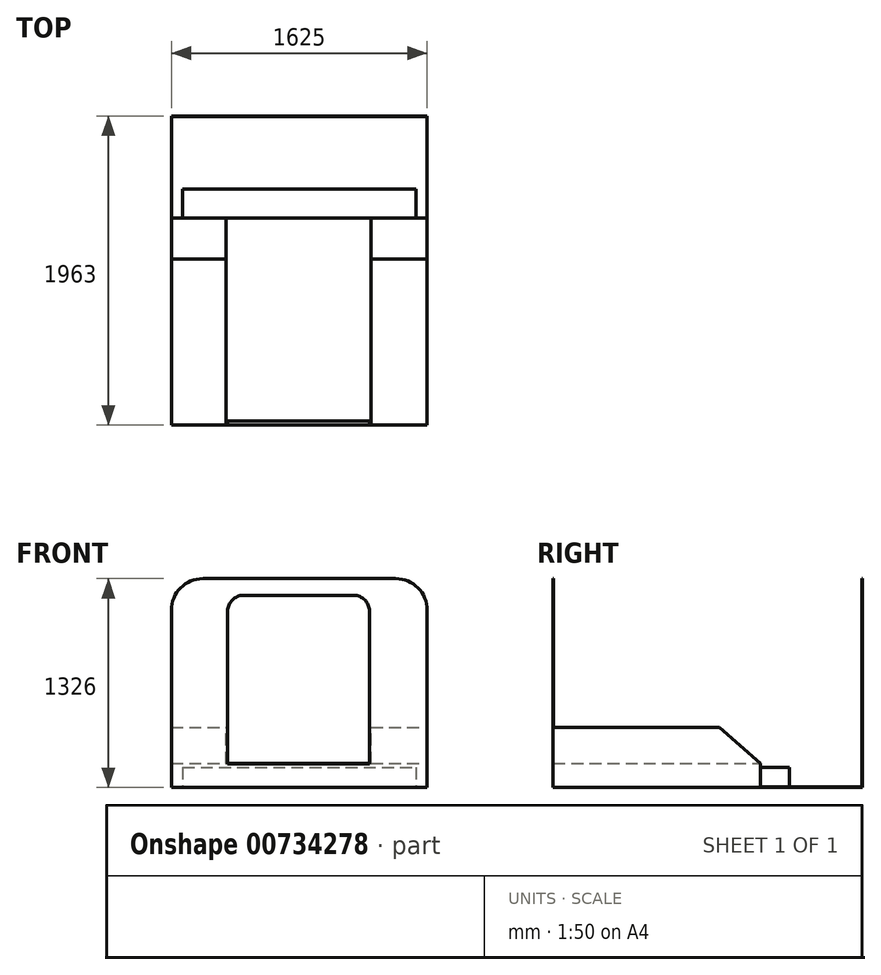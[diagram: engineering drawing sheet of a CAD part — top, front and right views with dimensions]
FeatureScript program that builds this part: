
annotation { "Feature Type Name" : "Feature", "Feature Type Description" : "" }
export const myFeature = defineFeature(function(context is Context, id is Id, definition is map)
    precondition{}
    {
        {
            var Q0;
            Q0=qCreatedBy(makeId("Top.planeOp"),FACE);
            var sketch = newSketch(context, id + "F0", { "sketchPlane" : qUnion([Q0])});
            skLineSegment(sketch, "E0.bottom", {"start": v(0, 0) * mm, "end": v(1625, 0) * mm});
            skLineSegment(sketch, "E0.top", {"start": v(0, 1960) * mm, "end": v(1625, 1960) * mm});
            skLineSegment(sketch, "E0.left", {"start": v(0, 0) * mm, "end": v(0, 1960) * mm});
            skLineSegment(sketch, "E0.right", {"start": v(1625, 0) * mm, "end": v(1625, 1960) * mm});
            skSolve(sketch);
        }
        {
            var Q0;
            Q0 = qSketchRegion(id + "F0", true);
            extrude(context, id + "F1", {"entities" : qUnion([Q0]), "depth" : 380 * mm, "offsetDistance" : 25 * mm});
        }
        {
            var Q0;
            Q0=makeQuery(id+"F1.opExtrude","CAP_FACE",FACE,{"disambiguationData":[OSD([sQuery(id+"F0.wireOp",EDGE,"E0.bottom"),sQuery(id+"F0.wireOp",EDGE,"E0.top"),sQuery(id+"F0.wireOp",EDGE,"E0.left"),sQuery(id+"F0.wireOp",EDGE,"E0.right")])],"isStart":false});
            var sketch = newSketch(context, id + "F2", { "sketchPlane" : qUnion([Q0])});
            skLineSegment(sketch, "E1.bottom", {"start": v(348, 0) * mm, "end": v(1268, 0) * mm});
            skLineSegment(sketch, "E1.top", {"start": v(348, 1960) * mm, "end": v(1268, 1960) * mm});
            skLineSegment(sketch, "E1.left", {"start": v(348, 0) * mm, "end": v(348, 1960) * mm});
            skLineSegment(sketch, "E1.right", {"start": v(1268, 0) * mm, "end": v(1268, 1960) * mm});
            skSolve(sketch);
        }
        {
            var Q0;
            Q0 = qSketchRegion(id + "F2", true);
            extrude(context, id + "F3", {"entities" : qUnion([Q0]), "operationType" : NewBodyOperationType.REMOVE, "oppositeDirection" : true, "depth" : 228 * mm, "offsetDistance" : 25 * mm});
        }
        {
            var Q0;
            {var subQ0=sQuery(id+"F0.wireOp",EDGE,"E0.bottom");var subQ1=sQuery(id+"F0.wireOp",EDGE,"E0.top");var subQ2=sQuery(id+"F0.wireOp",EDGE,"E0.left");Q0=makeQuery(id+"F3.boolean.opBoolean","SPLIT",FACE,{"disambiguationData":[TD([makeQuery(id+"F1.opExtrude","SWEPT_FACE",FACE,{"disambiguationData":[OSD([subQ2])]})])],"derivedFrom":makeQuery(id+"F1.opExtrude","CAP_FACE",FACE,{"disambiguationData":[OSD([subQ0,subQ1,subQ2,sQuery(id+"F0.wireOp",EDGE,"E0.right")])],"isStart":false})});}
            var sketch = newSketch(context, id + "F4", { "sketchPlane" : qUnion([Q0])});
            skLineSegment(sketch, "E2.bottom", {"start": v(0, 1960) * mm, "end": v(1625, 1960) * mm});
            skLineSegment(sketch, "E2.top", {"start": v(0, 1315) * mm, "end": v(1625, 1315) * mm});
            skLineSegment(sketch, "E2.left", {"start": v(0, 1960) * mm, "end": v(0, 1315) * mm});
            skLineSegment(sketch, "E2.right", {"start": v(1625, 1960) * mm, "end": v(1625, 1315) * mm});
            skSolve(sketch);
        }
        {
            var Q0;
            Q0 = qSketchRegion(id + "F4", true);
            extrude(context, id + "F5", {"entities" : qUnion([Q0]), "operationType" : NewBodyOperationType.REMOVE, "oppositeDirection" : true, "depth" : 378 * mm, "offsetDistance" : 25 * mm});
        }
        {
            var Q0;
            Q0=makeQuery(id+"F5.boolean.opBoolean","COPY",FACE,{"derivedFrom":makeQuery(id+"F5.opExtrude","CAP_FACE",FACE,{"disambiguationData":[OSD([sQuery(id+"F4.wireOp",EDGE,"E2.bottom"),sQuery(id+"F4.wireOp",EDGE,"E2.top"),sQuery(id+"F4.wireOp",EDGE,"E2.left"),sQuery(id+"F4.wireOp",EDGE,"E2.right")])],"isStart":false})});
            var sketch = newSketch(context, id + "F6", { "sketchPlane" : qUnion([Q0])});
            skLineSegment(sketch, "E3.bottom", {"start": v(72.5, 1315) * mm, "end": v(1552.5, 1315) * mm});
            skLineSegment(sketch, "E3.top", {"start": v(72.5, 1500) * mm, "end": v(1552.5, 1500) * mm});
            skLineSegment(sketch, "E3.left", {"start": v(72.5, 1315) * mm, "end": v(72.5, 1500) * mm});
            skLineSegment(sketch, "E3.right", {"start": v(1552.5, 1315) * mm, "end": v(1552.5, 1500) * mm});
            skSolve(sketch);
        }
        {
            var Q0;
            Q0 = qSketchRegion(id + "F6", true);
            extrude(context, id + "F7", {"entities" : qUnion([Q0]), "operationType" : NewBodyOperationType.ADD, "depth" : 125 * mm, "offsetDistance" : 25 * mm});
        }
        {
            var Q0;
            Q0=makeQuery(id+"F1.opExtrude","SWEPT_FACE",FACE,{"disambiguationData":[OSD([sQuery(id+"F0.wireOp",EDGE,"E0.top")])]});
            var sketch = newSketch(context, id + "F8", { "sketchPlane" : qUnion([Q0])});
            skLineSegment(sketch, "E4.bottom", {"start": v(-1625, 0) * mm, "end": v(0, 0) * mm});
            skLineSegment(sketch, "E4.top", {"start": v(-1425, 1326) * mm, "end": v(-200, 1326) * mm});
            skLineSegment(sketch, "E4.left", {"start": v(-1625, 0) * mm, "end": v(-1625, 1126) * mm});
            skLineSegment(sketch, "E4.right", {"start": v(0, 0) * mm, "end": v(0, 1126) * mm});
            skPoint(sketch, "E5.visualSharp", {"position": v(0, 1326) * mm});
            skArc(sketch, "E5.filletArc", {"start": v(0, 1126) * mm, "mid": v(-58.58, 1267.42) * mm, "end": v(-200, 1326) * mm});
            skPoint(sketch, "E6.visualSharp", {"position": v(-1625, 1326) * mm});
            skArc(sketch, "E6.filletArc", {"start": v(-1425, 1326) * mm, "mid": v(-1566.42, 1267.42) * mm, "end": v(-1625, 1126) * mm});
            skSolve(sketch);
        }
        {
            var Q0;
            Q0 = qSketchRegion(id + "F8", true);
            extrude(context, id + "F9", {"entities" : qUnion([Q0]), "operationType" : NewBodyOperationType.ADD, "depth" : 2 * mm, "offsetDistance" : 25 * mm});
        }
        {
            var Q0;
            Q0=makeQuery(id+"F1.opExtrude","SWEPT_FACE",FACE,{"disambiguationData":[OSD([sQuery(id+"F0.wireOp",EDGE,"E0.bottom")])]});
            var sketch = newSketch(context, id + "F10", { "sketchPlane" : qUnion([Q0])});
            skLineSegment(sketch, "E7.bottom", {"start": v(0, 0) * mm, "end": v(1625, 0) * mm});
            skLineSegment(sketch, "E7.top", {"start": v(200, 1326) * mm, "end": v(1425, 1326) * mm});
            skLineSegment(sketch, "E7.left", {"start": v(0, 0) * mm, "end": v(0, 1126) * mm});
            skLineSegment(sketch, "E7.right", {"start": v(1625, 0) * mm, "end": v(1625, 1126) * mm});
            skPoint(sketch, "E8.visualSharp", {"position": v(1625, 1326) * mm});
            skArc(sketch, "E8.filletArc", {"start": v(1625, 1126) * mm, "mid": v(1566.42, 1267.42) * mm, "end": v(1425, 1326) * mm});
            skPoint(sketch, "E9.visualSharp", {"position": v(0, 1326) * mm});
            skArc(sketch, "E9.filletArc", {"start": v(200, 1326) * mm, "mid": v(58.58, 1267.42) * mm, "end": v(0, 1126) * mm});
            skSolve(sketch);
        }
        {
            var Q0;
            Q0 = qSketchRegion(id + "F10", true);
            extrude(context, id + "F11", {"entities" : qUnion([Q0]), "operationType" : NewBodyOperationType.ADD, "depth" : 1 * mm, "offsetDistance" : 25 * mm});
        }
        {
            var Q0;
            Q0=makeQuery(id+"F11.opExtrude","CAP_FACE",FACE,{"disambiguationData":[OSD([sQuery(id+"F10.wireOp",EDGE,"E7.bottom"),sQuery(id+"F10.wireOp",EDGE,"E7.top"),sQuery(id+"F10.wireOp",EDGE,"E7.left"),sQuery(id+"F10.wireOp",EDGE,"E7.right"),sQuery(id+"F10.wireOp",EDGE,"E8.filletArc"),sQuery(id+"F10.wireOp",EDGE,"E9.filletArc")])],"isStart":false});
            var sketch = newSketch(context, id + "F12", { "sketchPlane" : qUnion([Q0])});
            skLineSegment(sketch, "E10.bottom", {"start": v(358, 150) * mm, "end": v(1258, 150) * mm});
            skLineSegment(sketch, "E10.top", {"start": v(458, 1220) * mm, "end": v(1158, 1220) * mm});
            skLineSegment(sketch, "E10.left", {"start": v(358, 150) * mm, "end": v(358, 1120) * mm});
            skLineSegment(sketch, "E10.right", {"start": v(1258, 150) * mm, "end": v(1258, 1120) * mm});
            skPoint(sketch, "E11.visualSharp", {"position": v(358, 1220) * mm});
            skArc(sketch, "E11.filletArc", {"start": v(458, 1220) * mm, "mid": v(387.29, 1190.71) * mm, "end": v(358, 1120) * mm});
            skPoint(sketch, "E12.visualSharp", {"position": v(1258, 1220) * mm});
            skArc(sketch, "E12.filletArc", {"start": v(1258, 1120) * mm, "mid": v(1228.71, 1190.71) * mm, "end": v(1158, 1220) * mm});
            skSolve(sketch);
        }
        {
            var Q0;
            Q0 = qSketchRegion(id + "F12", true);
            extrude(context, id + "F13", {"entities" : qUnion([Q0]), "operationType" : NewBodyOperationType.REMOVE, "oppositeDirection" : true, "depth" : 25 * mm, "offsetDistance" : 25 * mm});
        }
        {
            var Q0;
            Q0=makeQuery(id+"F11.boolean.opBoolean","MERGE",FACE,{"derivedFrom":[makeQuery(id+"F9.boolean.opBoolean","MERGE",FACE,{"derivedFrom":[makeQuery(id+"F1.opExtrude","SWEPT_FACE",FACE,{"disambiguationData":[OSD([sQuery(id+"F0.wireOp",EDGE,"E0.right")])]}),makeQuery(id+"F9.opExtrude","SWEPT_FACE",FACE,{"disambiguationData":[OSD([sQuery(id+"F8.wireOp",EDGE,"E4.left")])]})]}),makeQuery(id+"F11.opExtrude","SWEPT_FACE",FACE,{"disambiguationData":[OSD([sQuery(id+"F10.wireOp",EDGE,"E7.right")])]})]});
            var sketch = newSketch(context, id + "F14", { "sketchPlane" : qUnion([Q0])});
            skLineSegment(sketch, "E13", {"start": v(1315, 0) * mm, "end": v(1315, 152) * mm, "construction": true});
            skLineSegment(sketch, "E14", {"start": v(1315, 152) * mm, "end": v(1055, 152) * mm, "construction": true});
            skLineSegment(sketch, "E15", {"start": v(1055, 152) * mm, "end": v(1055, 380) * mm, "construction": true});
            skLineSegment(sketch, "E16", {"start": v(1055, 380) * mm, "end": v(1315, 152) * mm});
            skLineSegment(sketch, "E17", {"start": v(1055, 380) * mm, "end": v(1315, 380) * mm});
            skLineSegment(sketch, "E18", {"start": v(1315, 380) * mm, "end": v(1315, 152) * mm});
            skSolve(sketch);
        }
        {
            var Q0;
            Q0 = qSketchRegion(id + "F14", true);
            extrude(context, id + "F15", {"entities" : qUnion([Q0]), "operationType" : NewBodyOperationType.REMOVE, "endBound" : BoundingType.THROUGH_ALL, "oppositeDirection" : true, "depth" : 25 * mm, "offsetDistance" : 25 * mm});
        }
        {
            var Q0;
            Q0=makeQuery(id+"F11.boolean.opBoolean","MERGE",FACE,{"derivedFrom":[makeQuery(id+"F9.boolean.opBoolean","MERGE",FACE,{"derivedFrom":[makeQuery(id+"F1.opExtrude","SWEPT_FACE",FACE,{"disambiguationData":[OSD([sQuery(id+"F0.wireOp",EDGE,"E0.left")])]}),makeQuery(id+"F9.opExtrude","SWEPT_FACE",FACE,{"disambiguationData":[OSD([sQuery(id+"F8.wireOp",EDGE,"E4.right")])]})]}),makeQuery(id+"F11.opExtrude","SWEPT_FACE",FACE,{"disambiguationData":[OSD([sQuery(id+"F10.wireOp",EDGE,"E7.left")])]})]});
            var sketch = newSketch(context, id + "F16", { "sketchPlane" : qUnion([Q0])});
            skLineSegment(sketch, "E19", {"start": v(1, 1126) * mm, "end": v(-1960, 1126) * mm});
            skSolve(sketch);
        }
        {
            var Q0;
            Q0=makeQuery(id+"F11.opExtrude","CAP_FACE",FACE,{"disambiguationData":[OSD([sQuery(id+"F10.wireOp",EDGE,"E7.bottom"),sQuery(id+"F10.wireOp",EDGE,"E7.top"),sQuery(id+"F10.wireOp",EDGE,"E7.left"),sQuery(id+"F10.wireOp",EDGE,"E7.right"),sQuery(id+"F10.wireOp",EDGE,"E8.filletArc"),sQuery(id+"F10.wireOp",EDGE,"E9.filletArc")])],"isStart":false});
            var sketch = newSketch(context, id + "F17", { "sketchPlane" : qUnion([Q0])});
            skArc(sketch, "E20", {"start": v(200, 1326) * mm, "mid": v(58.58, 1267.42) * mm, "end": v(0, 1126) * mm});
            skSolve(sketch);
        }
        {
            var Q0;
            Q0=makeQuery(id+"F11.boolean.opBoolean","MERGE",FACE,{"derivedFrom":[makeQuery(id+"F9.boolean.opBoolean","MERGE",FACE,{"derivedFrom":[makeQuery(id+"F1.opExtrude","SWEPT_FACE",FACE,{"disambiguationData":[OSD([sQuery(id+"F0.wireOp",EDGE,"E0.right")])]}),makeQuery(id+"F9.opExtrude","SWEPT_FACE",FACE,{"disambiguationData":[OSD([sQuery(id+"F8.wireOp",EDGE,"E4.left")])]})]}),makeQuery(id+"F11.opExtrude","SWEPT_FACE",FACE,{"disambiguationData":[OSD([sQuery(id+"F10.wireOp",EDGE,"E7.right")])]})]});
            var sketch = newSketch(context, id + "F18", { "sketchPlane" : qUnion([Q0])});
            skLineSegment(sketch, "E21", {"start": v(0, 1126) * mm, "end": v(1960, 1126) * mm});
            skSolve(sketch);
        }
    });
